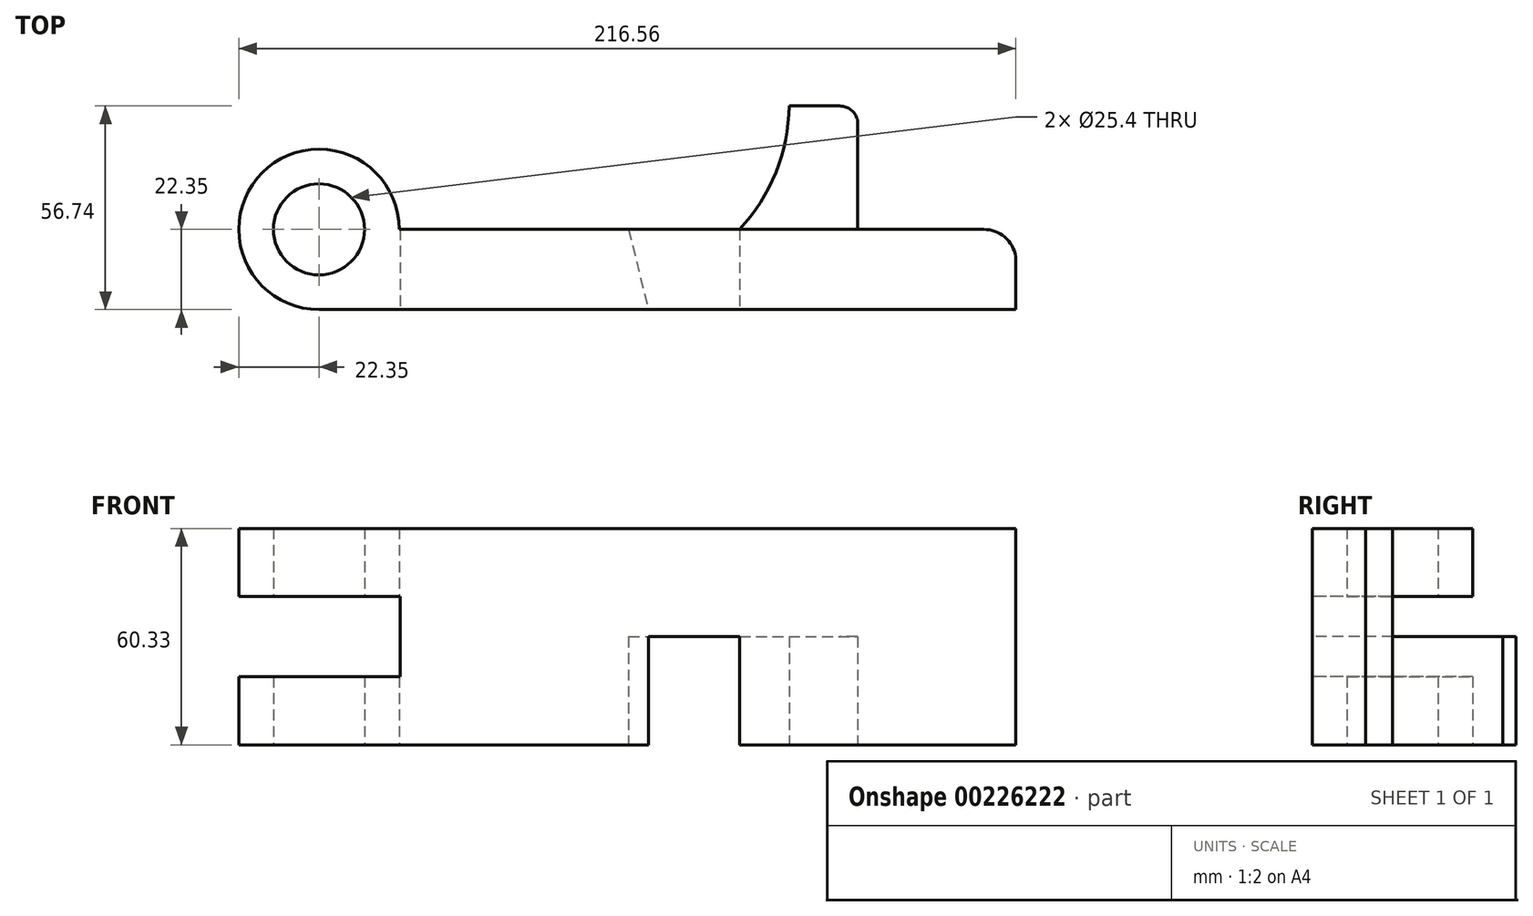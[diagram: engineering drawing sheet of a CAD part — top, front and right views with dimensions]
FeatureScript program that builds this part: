
annotation { "Feature Type Name" : "Feature", "Feature Type Description" : "" }
export const myFeature = defineFeature(function(context is Context, id is Id, definition is map)
    precondition{}
    {
        {
            var Q0;
            Q0=qCreatedBy(makeId("Top.planeOp"),FACE);
            var sketch = newSketch(context, id + "F0", { "sketchPlane" : qUnion([Q0])});
            skArc(sketch, "E0", {"start": v(22.35, 0) * mm, "mid": v(-15.8, 15.8) * mm, "end": v(0, -22.35) * mm});
            skCircle(sketch, "E1", {"center": v(0, 0) * mm, "radius": 12.7 * mm});
            skLineSegment(sketch, "E2.top", {"start": v(0, -22.35) * mm, "end": v(194.2, -22.35) * mm});
            skLineSegment(sketch, "E3", {"start": v(85.85, 0) * mm, "end": v(91.85, -22.35) * mm});
            skLineSegment(sketch, "E4.trimOffspring", {"start": v(22.35, 0) * mm, "end": v(117.25, 0) * mm});
            skLineSegment(sketch, "E5", {"start": v(117.25, 0) * mm, "end": v(117.25, -22.35) * mm});
            skLineSegment(sketch, "E6.bottom", {"start": v(150.09, 0) * mm, "end": v(162.98, 0) * mm});
            skPoint(sketch, "E7.start.orphan", {"position": v(131.04, 28.44) * mm});
            skArc(sketch, "E8", {"start": v(117.25, 0) * mm, "mid": v(127.39, 15.9) * mm, "end": v(131.04, 34.4) * mm});
            skLineSegment(sketch, "E9", {"start": v(150.09, 0) * mm, "end": v(150.09, 30.67) * mm});
            skLineSegment(sketch, "E10", {"start": v(131.04, 34.4) * mm, "end": v(145.2, 34.4) * mm});
            skArc(sketch, "E11", {"start": v(150.09, 30.67) * mm, "mid": v(148.27, 33.35) * mm, "end": v(145.2, 34.4) * mm});
            skLineSegment(sketch, "E12", {"start": v(194.2, -22.35) * mm, "end": v(194.2, -7.57) * mm});
            skLineSegment(sketch, "E13", {"start": v(162.98, 0) * mm, "end": v(185.33, 0) * mm});
            skArc(sketch, "E14", {"start": v(194.2, -7.57) * mm, "mid": v(191.16, -2.15) * mm, "end": v(185.33, 0) * mm});
            skLineSegment(sketch, "E15", {"start": v(117.25, 0) * mm, "end": v(150.09, 0) * mm});
            skSolve(sketch);
        }
        {
            var Q0;
            {var subQ2=sQuery(id+"F0.wireOp",EDGE,"E0");Q0=makeQuery(id+"F0.imprint","IMPRINT",FACE,{"disambiguationData":[TD([[makeQuery(id+"F0.imprint","IMPRINT",EDGE,{"derivedFrom":subQ2}),1.0]])]});}
            var Q1;
            {var subQ0=sQuery(id+"F0.wireOp",EDGE,"E3");Q1=makeQuery(id+"F0.imprint","IMPRINT",FACE,{"disambiguationData":[TD([[makeQuery(id+"F0.imprint","IMPRINT",EDGE,{"derivedFrom":subQ0}),1.0]])]});}
            var Q2;
            {var subQ1=sQuery(id+"F0.wireOp",EDGE,"E5");Q2=makeQuery(id+"F0.imprint","IMPRINT",FACE,{"disambiguationData":[TD([[makeQuery(id+"F0.imprint","IMPRINT",EDGE,{"derivedFrom":subQ1}),1.0]])]});}
            extrude(context, id + "F1", {"entities" : qUnion([Q0, Q1, Q2]), "depth" : 60.32 * mm});
        }
        {
            var Q0;
            Q0 = qSketchRegion(id + "F0", true);
            extrude(context, id + "F2", {"entities" : qUnion([Q0]), "operationType" : NewBodyOperationType.ADD, "depth" : 30.16 * mm});
        }
        {
            var Q0;
            Q0=makeQuery(id+"F1.opExtrude","SWEPT_FACE",FACE,{"disambiguationData":[OSD([sQuery(id+"F0.wireOp",EDGE,"E2.top")])]});
            var sketch = newSketch(context, id + "F3", { "sketchPlane" : qUnion([Q0])});
            skLineSegment(sketch, "E16", {"start": v(22.69, -27.27) * mm, "end": v(22.69, 65.26) * mm, "construction": true});
            skPoint(sketch, "E17.middle", {"position": v(0, 30.16) * mm});
            skPoint(sketch, "E17.bottom.end.orphan", {"position": v(26.23, 33.93) * mm});
            skPoint(sketch, "E17.top.end.orphan", {"position": v(26.23, 26.4) * mm});
            skPoint(sketch, "E17.left.end.orphan", {"position": v(-26.23, 26.4) * mm});
            skPoint(sketch, "E17.left.start.orphan", {"position": v(-26.23, 33.93) * mm});
            skLineSegment(sketch, "E18.bottom", {"start": v(22.69, 19) * mm, "end": v(-31.94, 19) * mm});
            skLineSegment(sketch, "E18.top", {"start": v(22.69, 41.33) * mm, "end": v(-31.94, 41.33) * mm});
            skLineSegment(sketch, "E18.left", {"start": v(22.69, 19) * mm, "end": v(22.69, 41.33) * mm});
            skLineSegment(sketch, "E18.right", {"start": v(-31.94, 19) * mm, "end": v(-31.94, 41.33) * mm});
            skSolve(sketch);
        }
        {
            var Q0;
            {var subQ0=sQuery(id+"F3.wireOp",EDGE,"E18.right");Q0=makeQuery(id+"F3.imprint","IMPRINT",FACE,{"disambiguationData":[TD([[makeQuery(id+"F3.imprint","IMPRINT",EDGE,{"derivedFrom":subQ0}),-1.0]])]});}
            var Q1;
            {var subQ0=sQuery(id+"F3.wireOp",EDGE,"E18.left");Q1=makeQuery(id+"F3.imprint","IMPRINT",FACE,{"disambiguationData":[TD([[makeQuery(id+"F3.imprint","IMPRINT",EDGE,{"derivedFrom":subQ0}),1.0]])]});}
            extrude(context, id + "F4", {"entities" : qUnion([Q0, Q1]), "operationType" : NewBodyOperationType.REMOVE, "endBound" : BoundingType.THROUGH_ALL, "oppositeDirection" : true, "depth" : 25.4 * mm});
        }
        {
            var Q0;
            {var subQ0=sQuery(id+"F0.wireOp",EDGE,"E14");var subQ1=sQuery(id+"F0.wireOp",EDGE,"E13");var subQ2=sQuery(id+"F0.wireOp",EDGE,"E12");var subQ3=sQuery(id+"F0.wireOp",EDGE,"E6.bottom");var subQ4=sQuery(id+"F0.wireOp",EDGE,"E4.trimOffspring");var subQ5=sQuery(id+"F0.wireOp",EDGE,"E2.top");var subQ6=sQuery(id+"F0.wireOp",EDGE,"E1");var subQ7=sQuery(id+"F0.wireOp",EDGE,"E0");Q0=makeQuery(id+"F2.boolean.opBoolean","MERGE",FACE,{"derivedFrom":[makeQuery(id+"F1.opExtrude","CAP_FACE",FACE,{"disambiguationData":[OSD([subQ7,subQ6,subQ5,subQ4,subQ3,subQ2,subQ1,subQ0,sQuery(id+"F0.wireOp",EDGE,"E15")])],"isStart":true}),makeQuery(id+"F2.opExtrude","CAP_FACE",FACE,{"disambiguationData":[OSD([subQ7,subQ6,subQ5,subQ4,sQuery(id+"F0.wireOp",EDGE,"E8"),sQuery(id+"F0.wireOp",EDGE,"E9"),sQuery(id+"F0.wireOp",EDGE,"E10"),sQuery(id+"F0.wireOp",EDGE,"E11"),subQ3,subQ2,subQ1,subQ0])],"isStart":true})]});}
            var sketch = newSketch(context, id + "F5", { "sketchPlane" : qUnion([Q0])});
            skLineSegment(sketch, "E19", {"start": v(117.25, 0) * mm, "end": v(117.25, 22.35) * mm});
            skLineSegment(sketch, "E20", {"start": v(86.32, 0) * mm, "end": v(91.85, 22.35) * mm});
            skLineSegment(sketch, "E21", {"start": v(91.85, 22.35) * mm, "end": v(117.25, 22.35) * mm});
            skLineSegment(sketch, "E22", {"start": v(117.25, 0) * mm, "end": v(86.32, 0) * mm});
            skSolve(sketch);
        }
        {
            var Q0;
            Q0=makeQuery(id+"F5.imprint","IMPRINT",FACE,{"disambiguationData":[TD([[makeQuery(id+"F5.imprint","IMPRINT",EDGE,{"derivedFrom":sQuery(id+"F5.wireOp",EDGE,"E19")}),1.0]])]});
            extrude(context, id + "F6", {"entities" : qUnion([Q0]), "operationType" : NewBodyOperationType.REMOVE, "oppositeDirection" : true, "depth" : 30.16 * mm});
        }
    });
